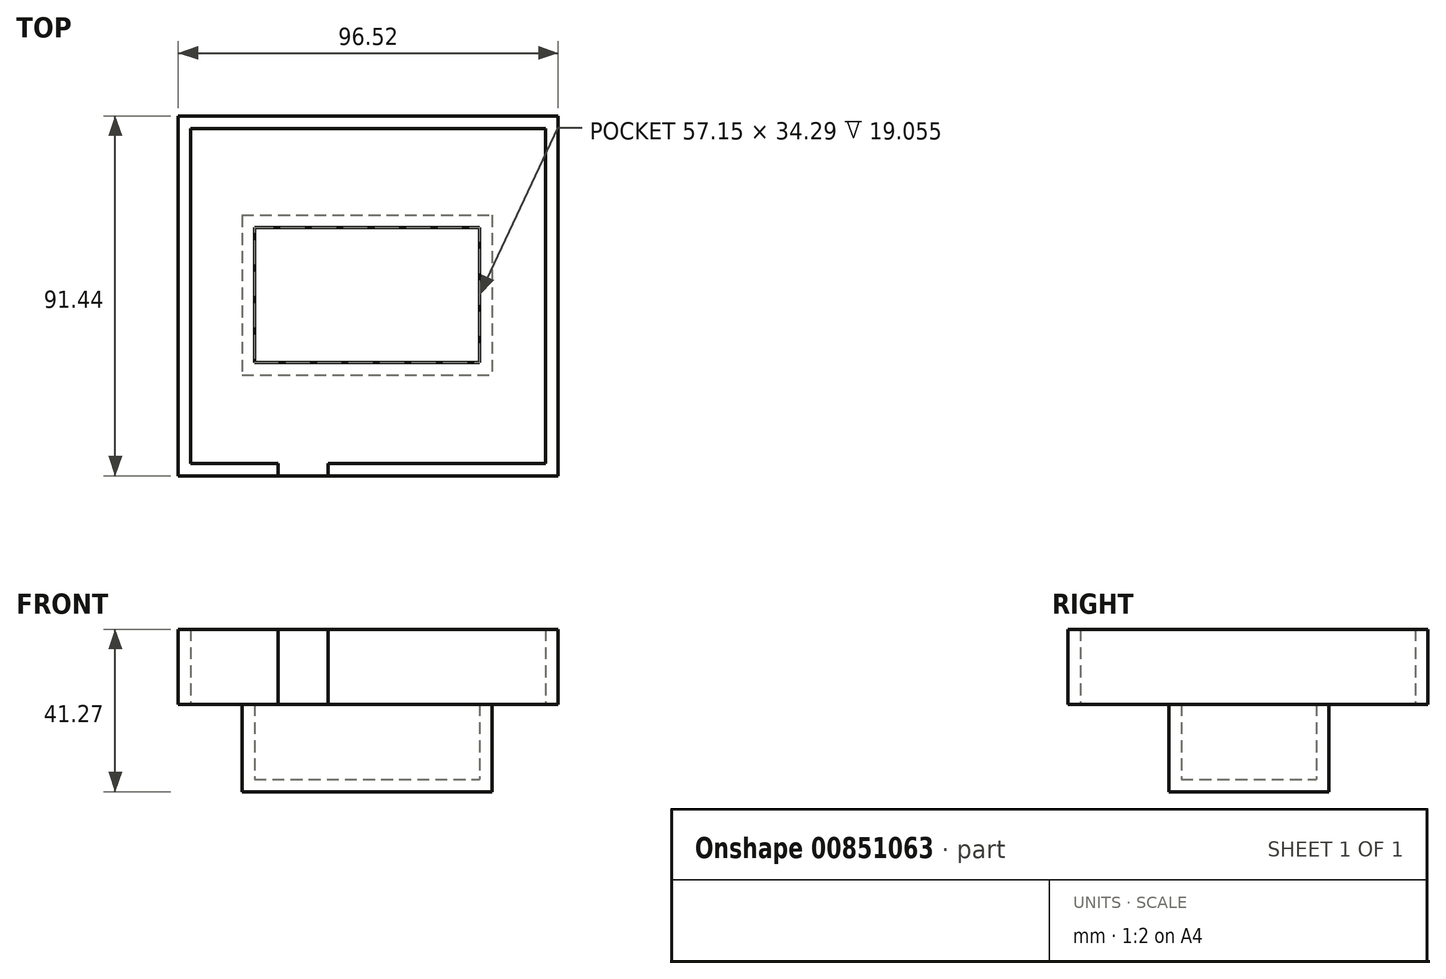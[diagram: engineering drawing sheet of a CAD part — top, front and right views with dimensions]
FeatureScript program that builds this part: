
annotation { "Feature Type Name" : "Feature", "Feature Type Description" : "" }
export const myFeature = defineFeature(function(context is Context, id is Id, definition is map)
    precondition{}
    {
        {
            var Q0;
            Q0=qCreatedBy(makeId("Top.planeOp"),FACE);
            var sketch = newSketch(context, id + "F0", { "sketchPlane" : qUnion([Q0])});
            skLineSegment(sketch, "E0.bottom", {"start": v(41.83, 84.7) * mm, "end": v(105.33, 84.7) * mm});
            skLineSegment(sketch, "E0.top", {"start": v(41.83, 44.05) * mm, "end": v(105.33, 44.05) * mm});
            skLineSegment(sketch, "E0.left", {"start": v(41.83, 84.7) * mm, "end": v(41.83, 44.05) * mm});
            skLineSegment(sketch, "E0.right", {"start": v(105.33, 84.7) * mm, "end": v(105.33, 44.05) * mm});
            skLineSegment(sketch, "E1", {"start": v(45, 47.23) * mm, "end": v(102.15, 47.23) * mm});
            skLineSegment(sketch, "E2", {"start": v(102.15, 47.23) * mm, "end": v(102.15, 81.52) * mm});
            skLineSegment(sketch, "E3.trimOffspring", {"start": v(45, 81.52) * mm, "end": v(102.15, 81.52) * mm});
            skLineSegment(sketch, "E4.trimOffspring", {"start": v(45, 47.23) * mm, "end": v(45, 81.52) * mm});
            skSolve(sketch);
        }
        {
            var Q0;
            Q0 = qSketchRegion(id + "F0", true);
            var Q1;
            Q1=makeQuery(id+"F0.imprint","IMPRINT",FACE,{"disambiguationData":[TD([[makeQuery(id+"F0.imprint","IMPRINT",EDGE,{"derivedFrom":sQuery(id+"F0.wireOp",EDGE,"E1")}),1.0]])]});
            extrude(context, id + "F1", {"entities" : qUnion([Q0, Q1]), "oppositeDirection" : true, "depth" : 3.17 * mm, "offsetDistance" : 25.4 * mm});
        }
        {
            var Q0;
            Q0 = qSketchRegion(id + "F0", true);
            extrude(context, id + "F2", {"entities" : qUnion([Q0]), "operationType" : NewBodyOperationType.ADD, "depth" : 19.05 * mm, "offsetDistance" : 25.4 * mm});
        }
        {
            var Q0;
            Q0=makeQuery(id+"F2.opExtrude","CAP_FACE",FACE,{"disambiguationData":[OSD([sQuery(id+"F0.wireOp",EDGE,"E0.bottom"),sQuery(id+"F0.wireOp",EDGE,"E0.top"),sQuery(id+"F0.wireOp",EDGE,"E0.left"),sQuery(id+"F0.wireOp",EDGE,"E0.right"),sQuery(id+"F0.wireOp",EDGE,"E1"),sQuery(id+"F0.wireOp",EDGE,"E2"),sQuery(id+"F0.wireOp",EDGE,"E3.trimOffspring"),sQuery(id+"F0.wireOp",EDGE,"E4.trimOffspring")])],"isStart":false});
            var sketch = newSketch(context, id + "F3", { "sketchPlane" : qUnion([Q0])});
            skLineSegment(sketch, "E5.bottom", {"start": v(45, 81.52) * mm, "end": v(102.15, 81.52) * mm});
            skLineSegment(sketch, "E5.top", {"start": v(45, 47.23) * mm, "end": v(102.15, 47.23) * mm});
            skLineSegment(sketch, "E5.left", {"start": v(45, 81.52) * mm, "end": v(45, 47.23) * mm});
            skLineSegment(sketch, "E5.right", {"start": v(102.15, 81.52) * mm, "end": v(102.15, 47.23) * mm});
            skLineSegment(sketch, "E6.top", {"start": v(25.65, 18.46) * mm, "end": v(122.17, 18.46) * mm});
            skLineSegment(sketch, "E6.left", {"start": v(25.65, 109.9) * mm, "end": v(25.65, 18.46) * mm});
            skLineSegment(sketch, "E6.right", {"start": v(122.17, 109.9) * mm, "end": v(122.17, 18.46) * mm});
            skLineSegment(sketch, "E7", {"start": v(25.65, 109.9) * mm, "end": v(122.17, 109.9) * mm});
            skPoint(sketch, "E8.start.orphan", {"position": v(25.65, 115.43) * mm});
            skPoint(sketch, "E9.start.orphan", {"position": v(21.4, 109.9) * mm});
            skLineSegment(sketch, "E10.bottom", {"start": v(28.83, 106.72) * mm, "end": v(119, 106.72) * mm});
            skLineSegment(sketch, "E10.top", {"start": v(28.83, 21.63) * mm, "end": v(51.05, 21.63) * mm});
            skLineSegment(sketch, "E10.left", {"start": v(28.83, 106.72) * mm, "end": v(28.83, 21.63) * mm});
            skLineSegment(sketch, "E10.right", {"start": v(119, 106.72) * mm, "end": v(119, 21.63) * mm});
            skLineSegment(sketch, "E11", {"start": v(63.75, 18.46) * mm, "end": v(63.75, 21.63) * mm});
            skLineSegment(sketch, "E12", {"start": v(51.05, 18.46) * mm, "end": v(51.05, 21.63) * mm});
            skLineSegment(sketch, "E13.trimOffspring", {"start": v(63.75, 21.63) * mm, "end": v(119, 21.63) * mm});
            skSolve(sketch);
        }
        {
            var Q0;
            Q0 = qSketchRegion(id + "F3", true);
            extrude(context, id + "F4", {"entities" : qUnion([Q0]), "operationType" : NewBodyOperationType.ADD, "depth" : 1 / 203.2 * mm, "offsetDistance" : 25.4 * mm});
        }
        {
            var Q0;
            {var subQ1=sQuery(id+"F3.wireOp",EDGE,"E6.left");Q0=makeQuery(id+"F3.imprint","IMPRINT",FACE,{"disambiguationData":[TD([[makeQuery(id+"F3.imprint","IMPRINT",EDGE,{"derivedFrom":subQ1}),1.0]])]});}
            extrude(context, id + "F5", {"entities" : qUnion([Q0]), "operationType" : NewBodyOperationType.ADD, "depth" : 19.05 * mm, "offsetDistance" : 25.4 * mm});
        }
    });
